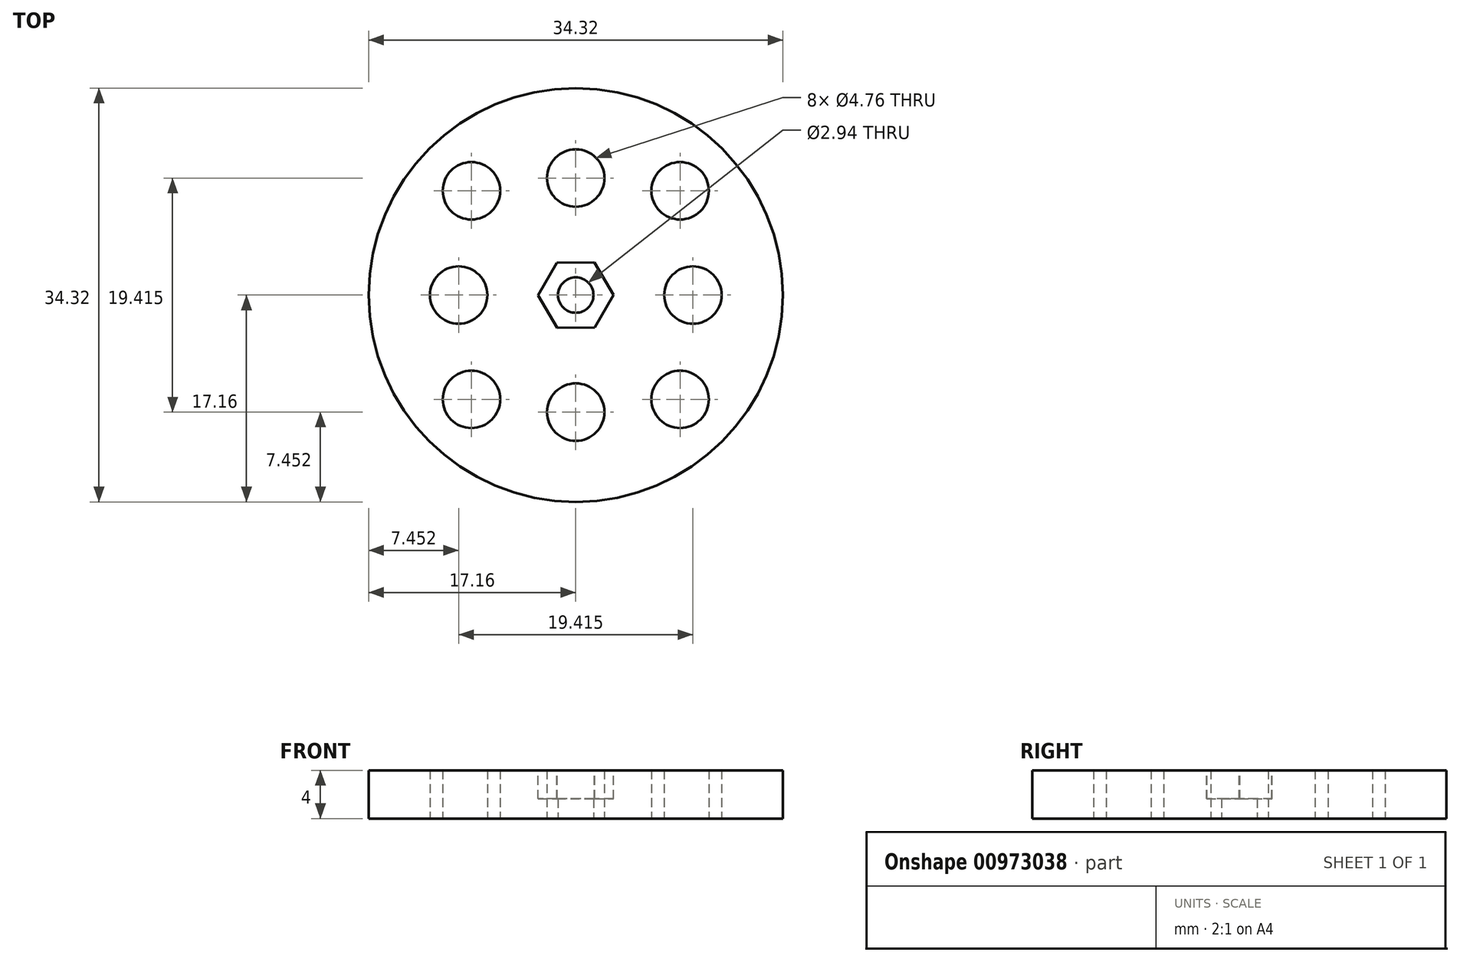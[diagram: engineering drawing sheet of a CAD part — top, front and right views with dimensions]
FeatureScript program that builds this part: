
annotation { "Feature Type Name" : "Feature", "Feature Type Description" : "" }
export const myFeature = defineFeature(function(context is Context, id is Id, definition is map)
    precondition{}
    {
        {
            var Q0;
            Q0=qCreatedBy(makeId("Top.planeOp"),FACE);
            var sketch = newSketch(context, id + "F0", { "sketchPlane" : qUnion([Q0])});
            skCircle(sketch, "E0", {"center": v(0, 0) * mm, "radius": 17.16 * mm});
            skCircle(sketch, "E1", {"center": v(0, 0) * mm, "radius": 1.47 * mm});
            skLineSegment(sketch, "E2", {"start": v(0, 17.16) * mm, "end": v(0, -17.16) * mm, "construction": true});
            skLineSegment(sketch, "E3", {"start": v(17.16, 0) * mm, "end": v(-17.16, 0) * mm, "construction": true});
            skCircle(sketch, "E4", {"center": v(0, 9.7) * mm, "radius": 2.38 * mm});
            skLineSegment(sketch, "E5", {"start": v(0, 17.16) * mm, "end": v(-12.13, 12.13) * mm, "construction": true});
            skLineSegment(sketch, "E6", {"start": v(-12.13, 12.13) * mm, "end": v(-17.16, 0) * mm, "construction": true});
            skLineSegment(sketch, "E7", {"start": v(-12.13, 12.13) * mm, "end": v(12.13, -12.13) * mm, "construction": true});
            skCircle(sketch, "E8", {"center": v(-8.65, 8.65) * mm, "radius": 2.38 * mm});
            skCircle(sketch, "E9.1.0", {"center": v(-9.7, 0) * mm, "radius": 2.38 * mm});
            skCircle(sketch, "E9.1.1", {"center": v(-8.65, -8.65) * mm, "radius": 2.38 * mm});
            skCircle(sketch, "E9.2.0", {"center": v(0, -9.7) * mm, "radius": 2.38 * mm});
            skCircle(sketch, "E9.2.1", {"center": v(8.65, -8.65) * mm, "radius": 2.38 * mm});
            skCircle(sketch, "E9.3.0", {"center": v(9.7, 0) * mm, "radius": 2.38 * mm});
            skCircle(sketch, "E9.3.1", {"center": v(8.65, 8.65) * mm, "radius": 2.38 * mm});
            skSolve(sketch);
        }
        {
            var Q0;
            Q0 = qSketchRegion(id + "F0", true);
            extrude(context, id + "F1", {"entities" : qUnion([Q0]), "depth" : 4 * mm, "offsetDistance" : 25 * mm});
        }
        {
            var Q0;
            Q0=makeQuery(id+"F1.opExtrude","CAP_FACE",FACE,{"disambiguationData":[OSD([sQuery(id+"F0.wireOp",EDGE,"E0"),sQuery(id+"F0.wireOp",EDGE,"E1"),sQuery(id+"F0.wireOp",EDGE,"E4"),sQuery(id+"F0.wireOp",EDGE,"E8"),sQuery(id+"F0.wireOp",EDGE,"E9.1.0"),sQuery(id+"F0.wireOp",EDGE,"E9.1.1"),sQuery(id+"F0.wireOp",EDGE,"E9.2.0"),sQuery(id+"F0.wireOp",EDGE,"E9.2.1"),sQuery(id+"F0.wireOp",EDGE,"E9.3.0"),sQuery(id+"F0.wireOp",EDGE,"E9.3.1")])],"isStart":false});
            var sketch = newSketch(context, id + "F2", { "sketchPlane" : qUnion([Q0])});
            skCircle(sketch, "E10.cCircle", {"center": v(0, 0) * mm, "radius": 2.7 * mm, "construction": true});
            skLineSegment(sketch, "E10.0", {"start": v(1.54, 2.71) * mm, "end": v(3.12, 0.02) * mm});
            skLineSegment(sketch, "E10.1", {"start": v(3.12, 0.02) * mm, "end": v(1.58, -2.69) * mm});
            skLineSegment(sketch, "E10.2", {"start": v(1.58, -2.69) * mm, "end": v(-1.54, -2.71) * mm});
            skLineSegment(sketch, "E10.3", {"start": v(-1.54, -2.71) * mm, "end": v(-3.12, -0.02) * mm});
            skLineSegment(sketch, "E10.4", {"start": v(-3.12, -0.02) * mm, "end": v(-1.58, 2.69) * mm});
            skLineSegment(sketch, "E10.5", {"start": v(-1.58, 2.69) * mm, "end": v(1.54, 2.71) * mm});
            skPoint(sketch, "E10.0.midPoint", {"position": v(2.33, 1.37) * mm});
            skSolve(sketch);
        }
        {
            var Q0;
            Q0=makeQuery(id+"F2.imprint","IMPRINT",FACE,{"disambiguationData":[TD([[makeQuery(id+"F2.imprint","IMPRINT",EDGE,{"derivedFrom":sQuery(id+"F2.wireOp",EDGE,"E10.0")}),-1.0]])]});
            extrude(context, id + "F3", {"entities" : qUnion([Q0]), "operationType" : NewBodyOperationType.REMOVE, "oppositeDirection" : true, "depth" : 2.37 * mm, "offsetDistance" : 25 * mm});
        }
    });
